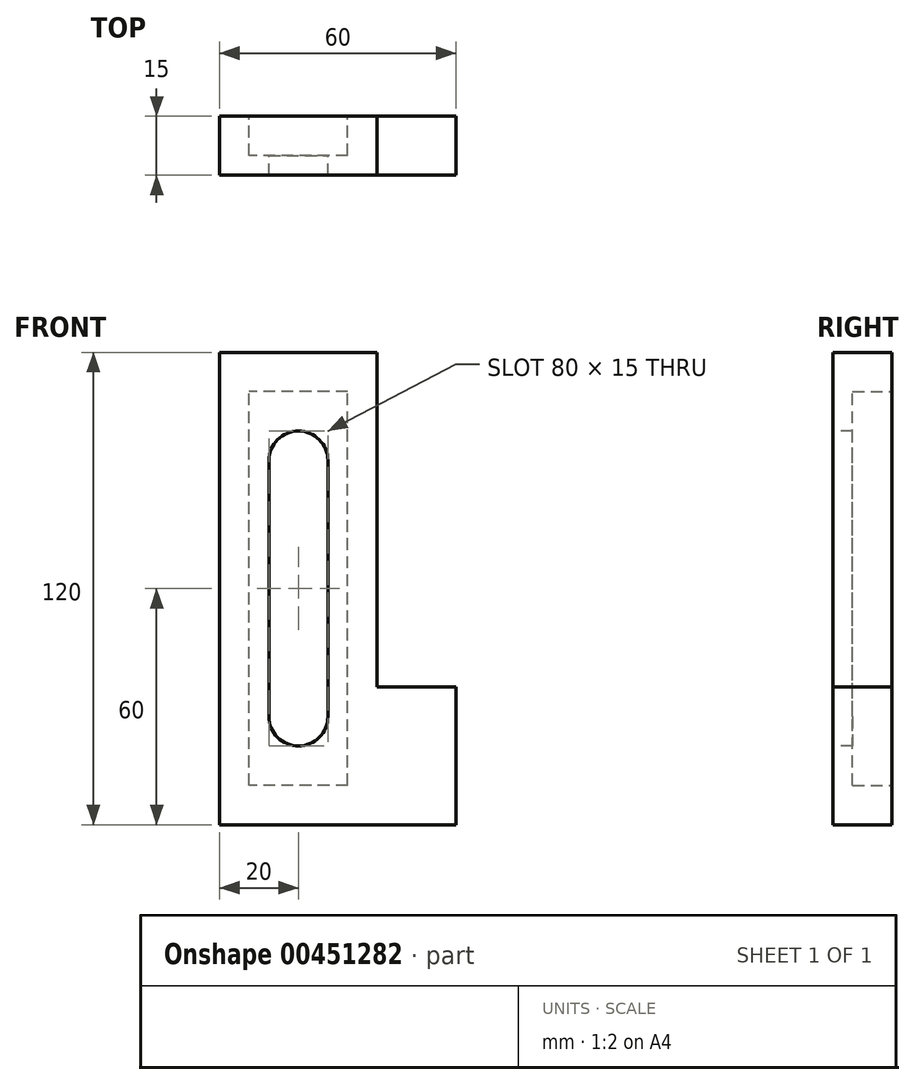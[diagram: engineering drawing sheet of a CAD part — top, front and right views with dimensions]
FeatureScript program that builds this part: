
annotation { "Feature Type Name" : "Feature", "Feature Type Description" : "" }
export const myFeature = defineFeature(function(context is Context, id is Id, definition is map)
    precondition{}
    {
        {
            var Q0;
            Q0=qCreatedBy(makeId("Front.planeOp"),FACE);
            var sketch = newSketch(context, id + "F0", { "sketchPlane" : qUnion([Q0])});
            skLineSegment(sketch, "E0.top", {"start": v(20, 60) * mm, "end": v(-20, 60) * mm});
            skLineSegment(sketch, "E0.left", {"start": v(20, -25) * mm, "end": v(20, 60) * mm});
            skLineSegment(sketch, "E0.right", {"start": v(-20, -60) * mm, "end": v(-20, 60) * mm});
            skPoint(sketch, "E0.middle", {"position": v(0, 0) * mm});
            skLineSegment(sketch, "E1.bottom", {"start": v(12.5, -50) * mm, "end": v(-12.5, -50) * mm});
            skLineSegment(sketch, "E1.top", {"start": v(12.5, 50) * mm, "end": v(-12.5, 50) * mm});
            skLineSegment(sketch, "E1.left", {"start": v(12.5, -50) * mm, "end": v(12.5, 50) * mm});
            skLineSegment(sketch, "E1.right", {"start": v(-12.5, -50) * mm, "end": v(-12.5, 50) * mm});
            skLineSegment(sketch, "E2.bottom", {"start": v(7.5, -40) * mm, "end": v(-7.5, -40) * mm});
            skLineSegment(sketch, "E2.top", {"start": v(7.5, 40) * mm, "end": v(-7.5, 40) * mm});
            skLineSegment(sketch, "E2.left", {"start": v(7.5, -40) * mm, "end": v(7.5, 40) * mm});
            skLineSegment(sketch, "E2.right", {"start": v(-7.5, -40) * mm, "end": v(-7.5, 40) * mm});
            skLineSegment(sketch, "E3", {"start": v(-20, -60) * mm, "end": v(40, -60) * mm});
            skPoint(sketch, "E4.orphan", {"position": v(-20, -60) * mm});
            skPoint(sketch, "E5.orphan", {"position": v(-40, -60) * mm});
            skLineSegment(sketch, "E6", {"start": v(20, -25) * mm, "end": v(40, -25) * mm});
            skLineSegment(sketch, "E7", {"start": v(40, -25) * mm, "end": v(40, -60) * mm});
            skPoint(sketch, "E8.orphan", {"position": v(20, -60) * mm});
            skSolve(sketch);
        }
        {
            var Q0;
            Q0=makeQuery(id+"F0.imprint","IMPRINT",FACE,{"disambiguationData":[TD([[makeQuery(id+"F0.imprint","IMPRINT",EDGE,{"derivedFrom":sQuery(id+"F0.wireOp",EDGE,"E0.top")}),1.0]])]});
            var Q1;
            Q1=makeQuery(id+"F0.imprint","IMPRINT",FACE,{"disambiguationData":[TD([[makeQuery(id+"F0.imprint","IMPRINT",EDGE,{"derivedFrom":sQuery(id+"F0.wireOp",EDGE,"E1.bottom")}),-1.0]])]});
            extrude(context, id + "F1", {"entities" : qUnion([Q0, Q1]), "depth" : 15 * mm});
        }
        {
            var Q0;
            Q0=makeQuery(id+"F0.imprint","IMPRINT",FACE,{"disambiguationData":[TD([[makeQuery(id+"F0.imprint","IMPRINT",EDGE,{"derivedFrom":sQuery(id+"F0.wireOp",EDGE,"E1.bottom")}),-1.0]])]});
            extrude(context, id + "F2", {"entities" : qUnion([Q0]), "operationType" : NewBodyOperationType.REMOVE, "depth" : 10 * mm});
        }
        {
            var Q0;
            Q0=makeQuery(id+"F1.opExtrude","SWEPT_EDGE",EDGE,{"disambiguationData":[OSD([sQuery(id+"F0.wireOp",EDGE,"E2.top"),sQuery(id+"F0.wireOp",EDGE,"E2.left")])]});
            var Q1;
            Q1=makeQuery(id+"F1.opExtrude","SWEPT_EDGE",EDGE,{"disambiguationData":[OSD([sQuery(id+"F0.wireOp",EDGE,"E2.top"),sQuery(id+"F0.wireOp",EDGE,"E2.right")])]});
            var Q2;
            Q2=makeQuery(id+"F1.opExtrude","SWEPT_EDGE",EDGE,{"disambiguationData":[OSD([sQuery(id+"F0.wireOp",EDGE,"E2.bottom"),sQuery(id+"F0.wireOp",EDGE,"E2.right")])]});
            var Q3;
            Q3=makeQuery(id+"F1.opExtrude","SWEPT_EDGE",EDGE,{"disambiguationData":[OSD([sQuery(id+"F0.wireOp",EDGE,"E2.bottom"),sQuery(id+"F0.wireOp",EDGE,"E2.left")])]});
            fillet(context, id + "F3", {"entities" : qUnion([Q0, Q1, Q2, Q3]), "radius" : 7.5 * mm, "tangentPropagation" : true, "allowEdgeOverflow" : false});
        }
    });
